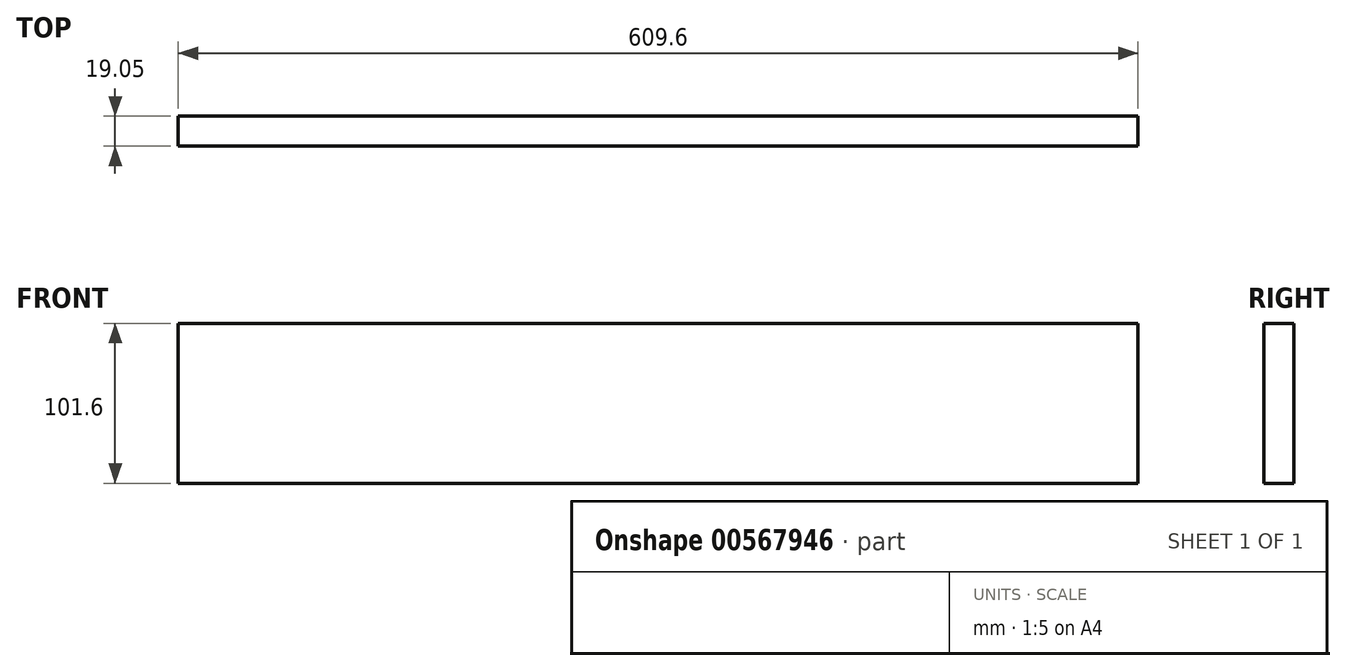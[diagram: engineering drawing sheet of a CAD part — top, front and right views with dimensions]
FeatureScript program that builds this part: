
annotation { "Feature Type Name" : "Feature", "Feature Type Description" : "" }
export const myFeature = defineFeature(function(context is Context, id is Id, definition is map)
    precondition{}
    {
        {
            var Q0;
            Q0=qCreatedBy(makeId("Front.planeOp"),FACE);
            var sketch = newSketch(context, id + "F0", { "sketchPlane" : qUnion([Q0])});
            skLineSegment(sketch, "E0.bottom", {"start": v(0, 0) * mm, "end": v(609.6, 0) * mm});
            skLineSegment(sketch, "E0.top", {"start": v(0, 101.6) * mm, "end": v(609.6, 101.6) * mm});
            skLineSegment(sketch, "E0.left", {"start": v(0, 0) * mm, "end": v(0, 101.6) * mm});
            skLineSegment(sketch, "E0.right", {"start": v(609.6, 0) * mm, "end": v(609.6, 101.6) * mm});
            skSolve(sketch);
        }
        {
            var Q0;
            Q0 = qSketchRegion(id + "F0", true);
            extrude(context, id + "F1", {"entities" : qUnion([Q0]), "depth" : 19.05 * mm, "offsetDistance" : 25.4 * mm});
        }
    });
